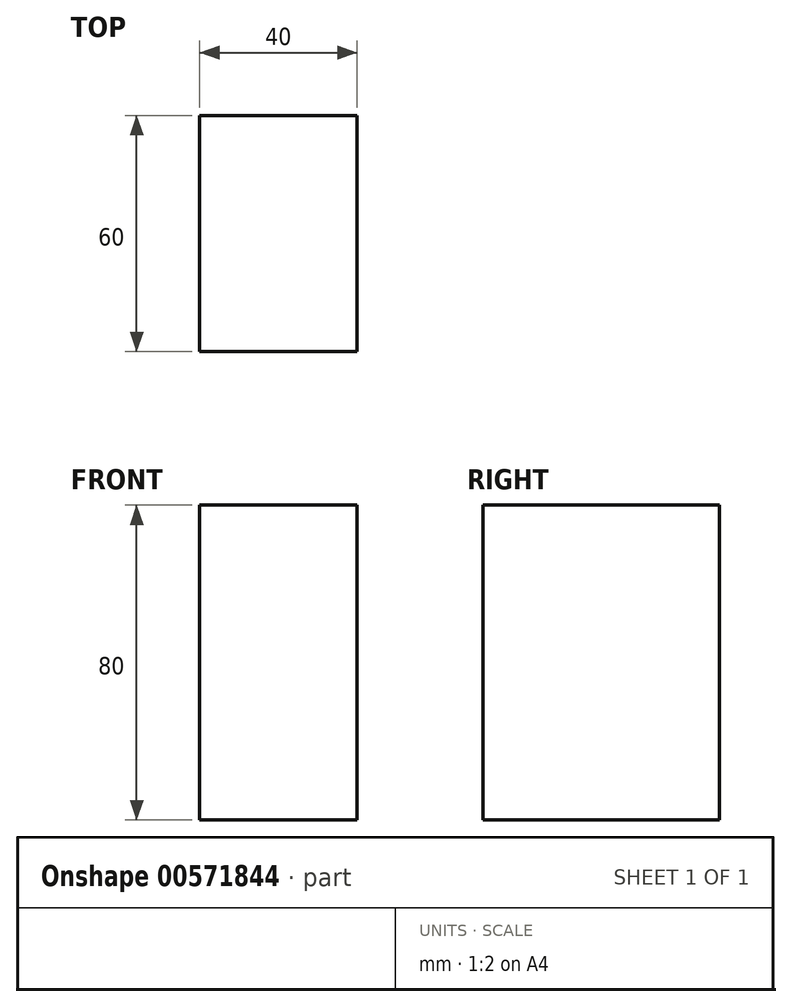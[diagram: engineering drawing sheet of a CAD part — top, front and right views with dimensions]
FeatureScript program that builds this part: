
annotation { "Feature Type Name" : "Feature", "Feature Type Description" : "" }
export const myFeature = defineFeature(function(context is Context, id is Id, definition is map)
    precondition{}
    {
        {
            var Q0;
            Q0=qCreatedBy(makeId("Top.planeOp"),FACE);
            var sketch = newSketch(context, id + "F0", { "sketchPlane" : qUnion([Q0])});
            skLineSegment(sketch, "E0.bottom", {"start": v(0, 0) * mm, "end": v(-40, 0) * mm});
            skLineSegment(sketch, "E0.top", {"start": v(0, 60) * mm, "end": v(-40, 60) * mm});
            skLineSegment(sketch, "E0.left", {"start": v(0, 0) * mm, "end": v(0, 60) * mm});
            skLineSegment(sketch, "E0.right", {"start": v(-40, 0) * mm, "end": v(-40, 60) * mm});
            skSolve(sketch);
        }
        {
            var Q0;
            Q0=makeQuery(id+"F0.imprint","IMPRINT",FACE,{"disambiguationData":[TD([[makeQuery(id+"F0.imprint","IMPRINT",EDGE,{"derivedFrom":sQuery(id+"F0.wireOp",EDGE,"E0.bottom")}),-1.0]])]});
            extrude(context, id + "F1", {"entities" : qUnion([Q0]), "depth" : 80 * mm, "offsetDistance" : 25 * mm});
        }
    });
